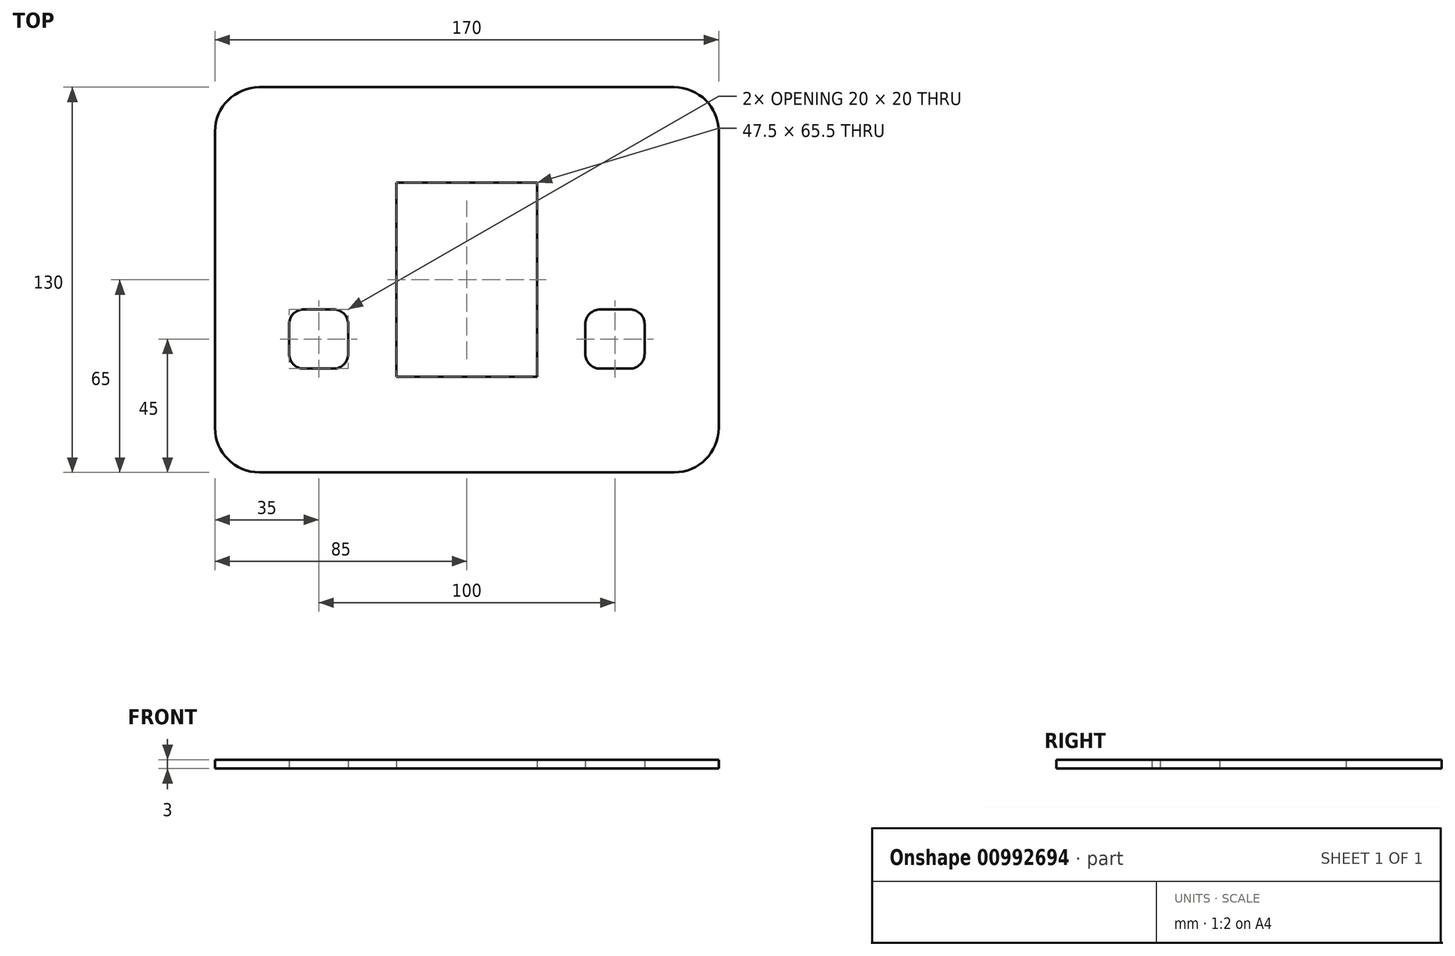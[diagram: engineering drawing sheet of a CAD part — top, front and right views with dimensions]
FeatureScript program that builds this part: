
annotation { "Feature Type Name" : "Feature", "Feature Type Description" : "" }
export const myFeature = defineFeature(function(context is Context, id is Id, definition is map)
    precondition{}
    {
        {
            var Q0;
            Q0=qCreatedBy(makeId("Top.planeOp"),FACE);
            var sketch = newSketch(context, id + "F0", { "sketchPlane" : qUnion([Q0])});
            skLineSegment(sketch, "E0.bottom", {"start": v(-70, 65) * mm, "end": v(70, 65) * mm});
            skLineSegment(sketch, "E0.top", {"start": v(-70, -65) * mm, "end": v(70, -65) * mm});
            skLineSegment(sketch, "E0.left", {"start": v(-85, 50) * mm, "end": v(-85, -50) * mm});
            skLineSegment(sketch, "E0.right", {"start": v(85, 50) * mm, "end": v(85, -50) * mm});
            skPoint(sketch, "E0.middle", {"position": v(0, 0) * mm});
            skPoint(sketch, "E1.visualSharp", {"position": v(-85, 65) * mm});
            skArc(sketch, "E1.filletArc", {"start": v(-70, 65) * mm, "mid": v(-80.6, 60.6) * mm, "end": v(-85, 50) * mm});
            skPoint(sketch, "E2.visualSharp", {"position": v(85, 65) * mm});
            skArc(sketch, "E2.filletArc", {"start": v(85, 50) * mm, "mid": v(80.6, 60.6) * mm, "end": v(70, 65) * mm});
            skPoint(sketch, "E3.visualSharp", {"position": v(85, -65) * mm});
            skArc(sketch, "E3.filletArc", {"start": v(70, -65) * mm, "mid": v(80.6, -60.6) * mm, "end": v(85, -50) * mm});
            skPoint(sketch, "E4.visualSharp", {"position": v(-85, -65) * mm});
            skArc(sketch, "E4.filletArc", {"start": v(-85, -50) * mm, "mid": v(-80.6, -60.6) * mm, "end": v(-70, -65) * mm});
            skLineSegment(sketch, "E5.bottom", {"start": v(-23.75, 32.75) * mm, "end": v(23.75, 32.75) * mm});
            skLineSegment(sketch, "E5.top", {"start": v(-23.75, -32.75) * mm, "end": v(23.75, -32.75) * mm});
            skLineSegment(sketch, "E5.left", {"start": v(-23.75, 32.75) * mm, "end": v(-23.75, -32.75) * mm});
            skLineSegment(sketch, "E5.right", {"start": v(23.75, 32.75) * mm, "end": v(23.75, -32.75) * mm});
            skLineSegment(sketch, "E6.bottom", {"start": v(-55, -10) * mm, "end": v(-45, -10) * mm});
            skLineSegment(sketch, "E6.top", {"start": v(-55, -30) * mm, "end": v(-45, -30) * mm});
            skLineSegment(sketch, "E6.left", {"start": v(-60, -15) * mm, "end": v(-60, -25) * mm});
            skLineSegment(sketch, "E6.right", {"start": v(-40, -15) * mm, "end": v(-40, -25) * mm});
            skPoint(sketch, "E6.middle", {"position": v(-50, -20) * mm});
            skPoint(sketch, "E7.visualSharp", {"position": v(-60, -10) * mm});
            skArc(sketch, "E7.filletArc", {"start": v(-55, -10) * mm, "mid": v(-58.54, -11.46) * mm, "end": v(-60, -15) * mm});
            skPoint(sketch, "E8.visualSharp", {"position": v(-40, -10) * mm});
            skArc(sketch, "E8.filletArc", {"start": v(-40, -15) * mm, "mid": v(-41.46, -11.46) * mm, "end": v(-45, -10) * mm});
            skPoint(sketch, "E9.visualSharp", {"position": v(-40, -30) * mm});
            skArc(sketch, "E9.filletArc", {"start": v(-45, -30) * mm, "mid": v(-41.46, -28.54) * mm, "end": v(-40, -25) * mm});
            skPoint(sketch, "E10.visualSharp", {"position": v(-60, -30) * mm});
            skArc(sketch, "E10.filletArc", {"start": v(-60, -25) * mm, "mid": v(-58.54, -28.54) * mm, "end": v(-55, -30) * mm});
            skArc(sketch, "E11.MirrorCS", {"start": v(55, -10) * mm, "mid": v(58.54, -11.46) * mm, "end": v(60, -15) * mm});
            skLineSegment(sketch, "E12.MirrorCS", {"start": v(55, -10) * mm, "end": v(45, -10) * mm});
            skArc(sketch, "E13.MirrorCS", {"start": v(40, -15) * mm, "mid": v(41.46, -11.46) * mm, "end": v(45, -10) * mm});
            skLineSegment(sketch, "E14.MirrorCS", {"start": v(40, -15) * mm, "end": v(40, -25) * mm});
            skArc(sketch, "E15.MirrorCS", {"start": v(45, -30) * mm, "mid": v(41.46, -28.54) * mm, "end": v(40, -25) * mm});
            skLineSegment(sketch, "E16.MirrorCS", {"start": v(55, -30) * mm, "end": v(45, -30) * mm});
            skArc(sketch, "E17.MirrorCS", {"start": v(60, -25) * mm, "mid": v(58.54, -28.54) * mm, "end": v(55, -30) * mm});
            skLineSegment(sketch, "E18.MirrorCS", {"start": v(60, -15) * mm, "end": v(60, -25) * mm});
            skSolve(sketch);
        }
        {
            var Q0;
            Q0=makeQuery(id+"F0.imprint","IMPRINT",FACE,{"disambiguationData":[TD([[makeQuery(id+"F0.imprint","IMPRINT",EDGE,{"derivedFrom":sQuery(id+"F0.wireOp",EDGE,"E0.bottom")}),-1.0]])]});
            extrude(context, id + "F1", {"entities" : qUnion([Q0]), "depth" : 3 * mm, "offsetDistance" : 25 * mm});
        }
    });
